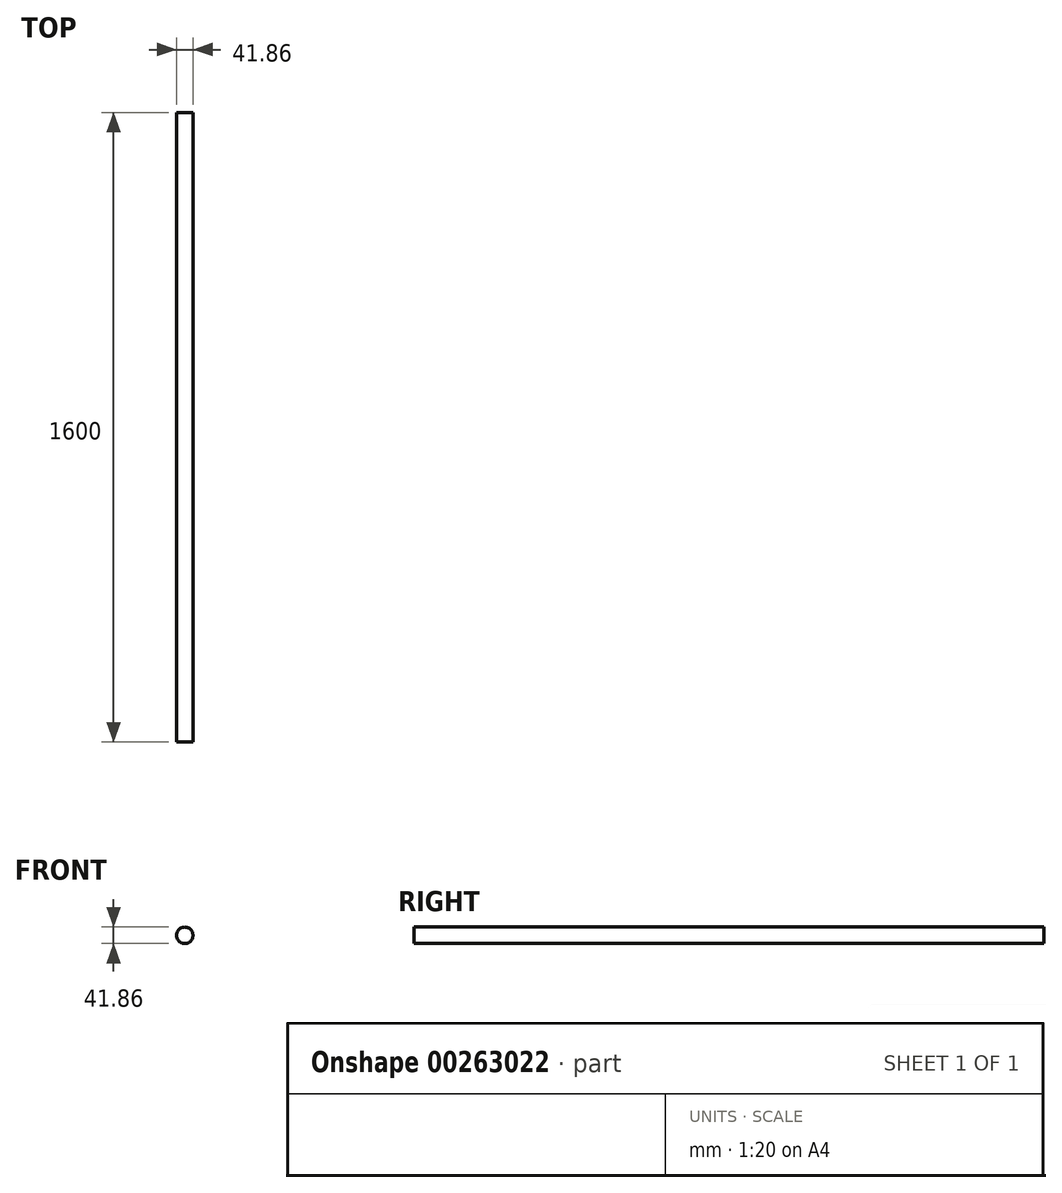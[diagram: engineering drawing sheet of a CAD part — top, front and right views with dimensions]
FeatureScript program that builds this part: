
annotation { "Feature Type Name" : "Feature", "Feature Type Description" : "" }
export const myFeature = defineFeature(function(context is Context, id is Id, definition is map)
    precondition{}
    {
        {
            var Q0;
            Q0=qCreatedBy(makeId("Front.planeOp"),FACE);
            var sketch = newSketch(context, id + "F0", { "sketchPlane" : qUnion([Q0])});
            skCircle(sketch, "E0", {"center": v(0, 0) * mm, "radius": 20.93 * mm});
            skSolve(sketch);
        }
        {
            var Q0;
            Q0=makeQuery(id+"F0.imprint","IMPRINT",FACE,{"disambiguationData":[TD([[makeQuery(id+"F0.imprint","IMPRINT",EDGE,{"derivedFrom":sQuery(id+"F0.wireOp",EDGE,"E0")}),1.0]])]});
            extrude(context, id + "F1", {"entities" : qUnion([Q0]), "depth" : 800 * mm, "hasSecondDirection" : true, "secondDirectionOppositeDirection" : true, "secondDirectionDepth" : 800 * mm});
        }
    });
